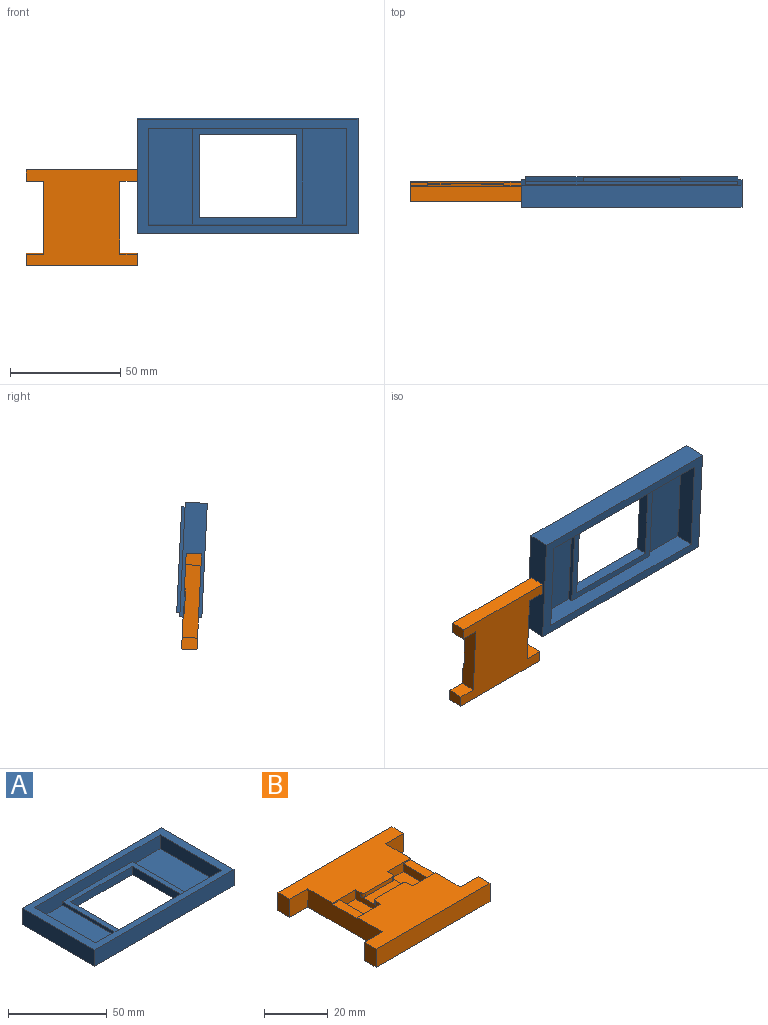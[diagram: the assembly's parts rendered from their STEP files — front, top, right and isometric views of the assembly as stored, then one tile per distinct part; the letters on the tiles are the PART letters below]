
ASSEMBLY  parts=2 mates=1
PART A: 24 faces, bbox 100x52x11.5 mm
  f0: plane 50x44mm, normal (0,0,1), area 528mm2, adj f1,f11,f12,f13,f18,f19,f20,f23
  f1: plane 90x8.5mm, normal (0,-1,0), area 665mm2, adj f0,f2,f6,f7,f11,f15,f16,f18
  f2: plane 100x52mm, normal (0,0,1), area 1240mm2, adj f1,f3,f4,f6,f14,f15,f20,f21
  f3: plane 52x10mm, normal (1,0,0), area 520mm2, adj f2,f4,f5,f21
  f4: plane 100x10mm, normal (0,1,0), area 1000mm2, adj f2,f3,f5,f14
  f5: plane 100x52mm, normal (0,0,-1), area 592mm2, adj f3,f4,f8,f9,f14,f17,f21,f22
  f6: plane 44x8.5mm, normal (-1,0,0), area 374mm2, adj f1,f2,f7,f20
  f7: plane 44x20mm, normal (0,0,1), area 880mm2, adj f1,f6,f11,f20
  f8: plane 96x1.5mm, normal (0,1,0), area 144mm2, adj f5,f9,f10,f17
  f9: plane 48x1.5mm, normal (1,0,0), area 72mm2, adj f5,f8,f10,f22
  f10: plane 96x48mm, normal (0,0,-1), area 2936mm2, adj f8,f9,f12,f13,f17,f19,f22,f23
  f11: plane 44x2mm, normal (1,0,0), area 88mm2, adj f0,f1,f7,f20
  f12: plane 44x5mm, normal (0,-1,0), area 220mm2, adj f0,f10,f13,f19
  f13: plane 38x5mm, normal (-1,0,0), area 190mm2, adj f0,f10,f12,f23
  f14: plane 52x10mm, normal (-1,0,0), area 520mm2, adj f2,f4,f5,f21
  f15: plane 44x8.5mm, normal (1,0,0), area 374mm2, adj f1,f2,f16,f20
  f16: plane 44x20mm, normal (0,0,1), area 880mm2, adj f1,f15,f18,f20
  f17: plane 48x1.5mm, normal (-1,0,0), area 72mm2, adj f5,f8,f10,f22
  f18: plane 44x2mm, normal (-1,0,0), area 88mm2, adj f0,f1,f16,f20
  f19: plane 38x5mm, normal (1,0,0), area 190mm2, adj f0,f10,f12,f23
  f20: plane 90x8.5mm, normal (0,1,0), area 665mm2, adj f0,f2,f6,f7,f11,f15,f16,f18
  f21: plane 100x10mm, normal (0,-1,0), area 1000mm2, adj f2,f3,f5,f14
  f22: plane 96x1.5mm, normal (0,-1,0), area 144mm2, adj f5,f9,f10,f17
  f23: plane 44x5mm, normal (0,1,0), area 220mm2, adj f0,f10,f13,f19
PART B: 34 faces, bbox 50.5x43.5x7 mm
  f0: plane 14x6.5mm, normal (0,0,1), area 63.9mm2, adj f9,f10,f13,f19,f20,f26,f29,f33
  f1: plane 7x5.25mm, normal (-1,0,0), area 36.8mm2, adj f2,f3,f4,f5
  f2: plane 50.5x7mm, normal (0,-1,0), area 353.5mm2, adj f1,f3,f4,f21
  f3: plane 50.5x19.5mm, normal (0,0,1), area 689.7mm2, adj f1,f2,f5,f6,f8,f9,f10,f13
  f4: plane 50.5x43.5mm, normal (0,0,-1), area 1668.7mm2, adj f1,f2,f5,f6,f14,f15,f17,f21
  f5: plane 8x7mm, normal (0,1,0), area 56mm2, adj f1,f3,f4,f6
  f6: plane 33x7mm, normal (-1,0,0), area 225.5mm2, adj f3,f4,f5,f8,f12,f16,f17,f18
  f7: plane 11x3mm, normal (1,0,0), area 33mm2, adj f8,f11,f12,f18
  f8: plane 10.25x3.5mm, normal (0,1,0), area 26.1mm2, adj f3,f6,f7,f9,f11,f12
  f9: plane 11x3.5mm, normal (-1,0,0), area 28.7mm2, adj f0,f3,f8,f11,f13,f16,f18,f20
  f10: plane 12x1.5mm, normal (0,1,0), area 18mm2, adj f0,f3,f13,f29
  f11: plane 11x7mm, normal (0,0,1), area 77mm2, adj f7,f8,f9,f18
  f12: plane 11x3.25mm, normal (0,0,1), area 35.7mm2, adj f6,f7,f8,f18
  f13: cylinder r=1mm len=1.5mm, axis (0,0,1), area 2.4mm2, adj f0,f3,f9,f10
  f14: plane 7x5.25mm, normal (-1,0,0), area 36.7mm2, adj f4,f15,f16,f17
  f15: plane 50.5x7mm, normal (0,1,0), area 353.5mm2, adj f4,f14,f16,f30
  f16: plane 50.5x19.5mm, normal (0,0,1), area 689.7mm2, adj f6,f9,f14,f15,f17,f18,f19,f20
  f17: plane 8x7mm, normal (0,-1,0), area 56mm2, adj f4,f6,f14,f16
  f18: plane 10.25x3.5mm, normal (0,-1,0), area 26.1mm2, adj f6,f7,f9,f11,f12,f16
  f19: plane 12x1.5mm, normal (0,-1,0), area 18mm2, adj f0,f16,f20,f33
  f20: cylinder r=1mm len=1.5mm, axis (0,0,1), area 2.4mm2, adj f0,f9,f16,f19
  f21: plane 7x5.25mm, normal (1,0,0), area 36.7mm2, adj f2,f3,f4,f22
  f22: plane 8x7mm, normal (0,1,0), area 56mm2, adj f3,f4,f21,f23
  f23: plane 33x7mm, normal (1,0,0), area 225.5mm2, adj f3,f4,f16,f22,f25,f28,f31,f32
  f24: plane 11x3mm, normal (-1,0,0), area 33mm2, adj f25,f27,f28,f32
  f25: plane 10.25x3.5mm, normal (0,1,0), area 26.1mm2, adj f3,f23,f24,f26,f27,f28
  f26: plane 11x3.5mm, normal (1,0,0), area 28.7mm2, adj f0,f3,f16,f25,f27,f29,f32,f33
  f27: plane 11x7mm, normal (0,0,1), area 77mm2, adj f24,f25,f26,f32
  f28: plane 11x3.25mm, normal (0,0,1), area 35.8mm2, adj f23,f24,f25,f32
  f29: cylinder r=1mm len=1.5mm, axis (0,0,1), area 2.4mm2, adj f0,f3,f10,f26
  f30: plane 7x5.25mm, normal (1,0,0), area 36.7mm2, adj f4,f15,f16,f31
  f31: plane 8x7mm, normal (0,-1,0), area 56mm2, adj f4,f16,f23,f30
  f32: plane 10.25x3.5mm, normal (0,-1,0), area 26.1mm2, adj f16,f23,f24,f26,f27,f28
  f33: cylinder r=1mm len=1.5mm, axis (0,0,1), area 2.4mm2, adj f0,f16,f19,f26
PLACE A rot(axis=(1,0,0),92.7deg) t=(21.49,22.72,90.26)mm
PLACE B rot(axis=(0,-0.69,-0.72),180deg) t=(-28.51,16.17,49.4)mm
MATE parallel B.f1 <-> A.f11  axis (1,0,0) through (-28.51,19.54,52.19)mm
